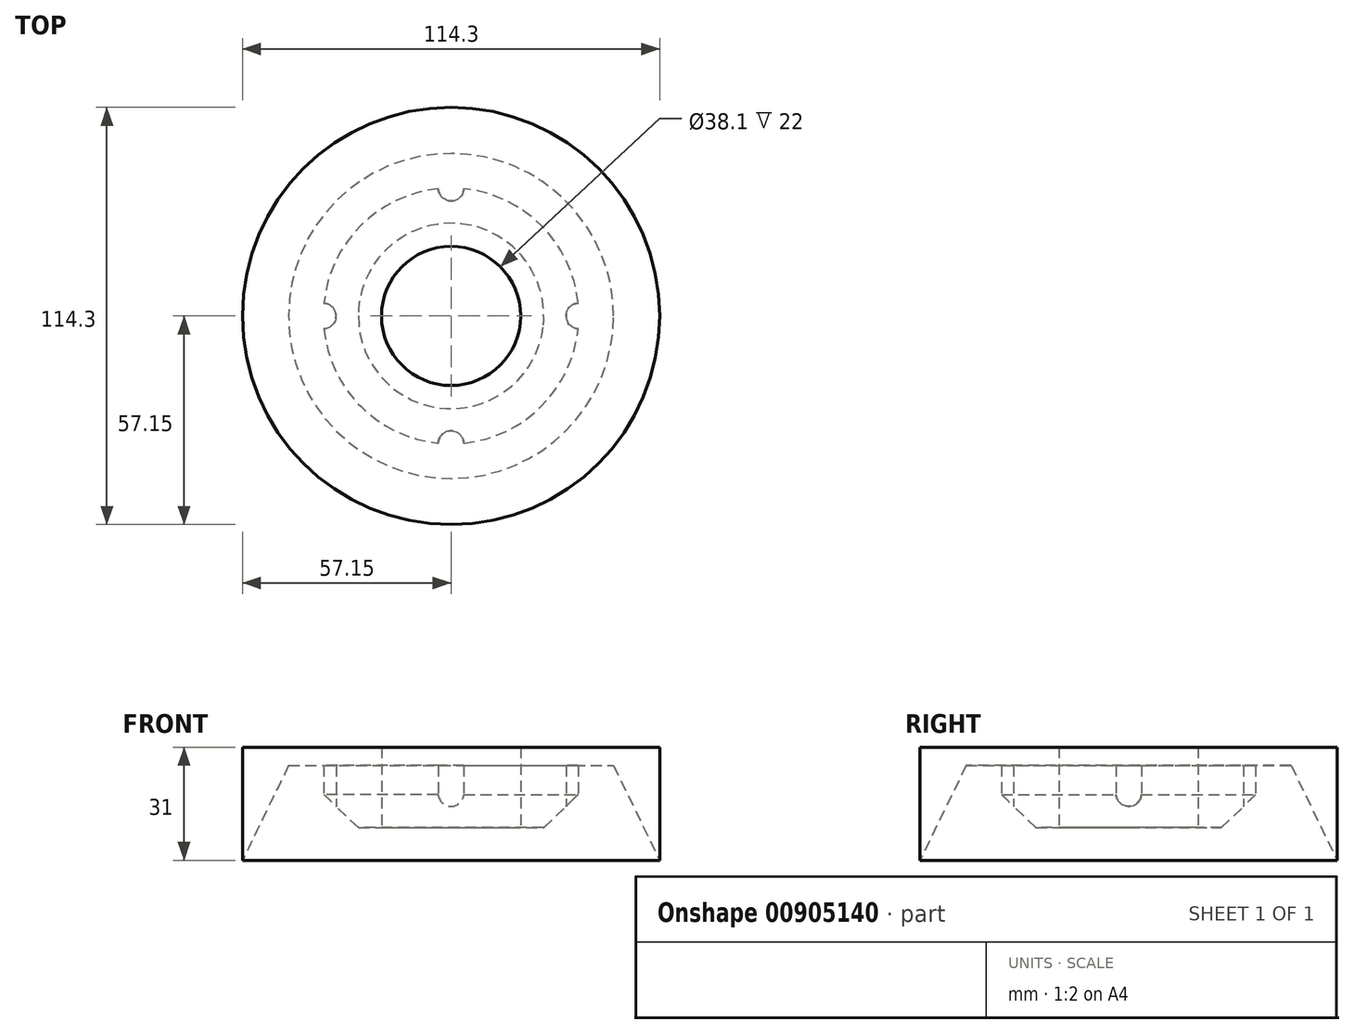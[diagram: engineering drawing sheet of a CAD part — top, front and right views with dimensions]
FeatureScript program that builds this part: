
annotation { "Feature Type Name" : "Feature", "Feature Type Description" : "" }
export const myFeature = defineFeature(function(context is Context, id is Id, definition is map)
    precondition{}
    {
        {
            var Q0;
            Q0=qCreatedBy(makeId("Front.planeOp"),FACE);
            var sketch = newSketch(context, id + "F0", { "sketchPlane" : qUnion([Q0])});
            skLineSegment(sketch, "E0", {"start": v(57.15, 0) * mm, "end": v(57.15, 31) * mm});
            skLineSegment(sketch, "E1", {"start": v(57.15, 31) * mm, "end": v(19.05, 31) * mm});
            skLineSegment(sketch, "E2", {"start": v(19.05, 31) * mm, "end": v(19.05, 9) * mm});
            skLineSegment(sketch, "E3", {"start": v(19.05, 9) * mm, "end": v(25.4, 9) * mm});
            skLineSegment(sketch, "E4", {"start": v(25.4, 9) * mm, "end": v(35, 18.06) * mm});
            skLineSegment(sketch, "E5", {"start": v(35, 18.06) * mm, "end": v(35, 26) * mm});
            skLineSegment(sketch, "E6", {"start": v(35, 26) * mm, "end": v(44.5, 26) * mm});
            skLineSegment(sketch, "E7", {"start": v(44.5, 26) * mm, "end": v(57.15, 0) * mm});
            skLineSegment(sketch, "E8", {"start": v(0, 0) * mm, "end": v(0, 38.1) * mm, "construction": true});
            skSolve(sketch);
        }
        {
            var Q0;
            Q0=makeQuery(id+"F0.imprint","IMPRINT",FACE,{"disambiguationData":[TD([[makeQuery(id+"F0.imprint","IMPRINT",EDGE,{"derivedFrom":sQuery(id+"F0.wireOp",EDGE,"E0")}),1.0]])]});
            var Q1;
            Q1=sQuery(id+"F0.wireOp",EDGE,"E8");
            revolve(context, id + "F1", {"surfaceOperationType" : NewSurfaceOperationType.NEW, "entities" : qUnion([Q0]), "axis" : qUnion([Q1]), "revolveType" : RevolveType.FULL});
        }
        {
            var Q0;
            Q0=makeQuery(id+"F1.opRevolve","SWEPT_FACE",FACE,{"disambiguationData":[OSD([sQuery(id+"F0.wireOp",EDGE,"E3")])]});
            var sketch = newSketch(context, id + "F2", { "sketchPlane" : qUnion([Q0])});
            skCircle(sketch, "E9", {"center": v(0, 35) * mm, "radius": 3.5 * mm});
            skLineSegment(sketch, "E10", {"start": v(0, 35) * mm, "end": v(0, 0) * mm, "construction": true});
            skCircle(sketch, "E11.1.0", {"center": v(-35, 0) * mm, "radius": 3.5 * mm});
            skCircle(sketch, "E11.2.0", {"center": v(0, -35) * mm, "radius": 3.5 * mm});
            skCircle(sketch, "E11.3.0", {"center": v(35, 0) * mm, "radius": 3.5 * mm});
            skPoint(sketch, "E11.center", {"position": v(0, 0) * mm});
            skSolve(sketch);
        }
        {
            var Q0;
            Q0 = qSketchRegion(id + "F2", true);
            var Q1;
            Q1=makeQuery(id+"F1.opRevolve","SWEPT_FACE",FACE,{"disambiguationData":[OSD([sQuery(id+"F0.wireOp",EDGE,"E6")])]});
            extrude(context, id + "F3", {"entities" : qUnion([Q0]), "operationType" : NewBodyOperationType.REMOVE, "endBound" : BoundingType.UP_TO_SURFACE, "oppositeDirection" : true, "depth" : 25.4 * mm, "endBoundEntityFace" : qUnion([Q1]), "offsetDistance" : 25.4 * mm});
        }
    });
